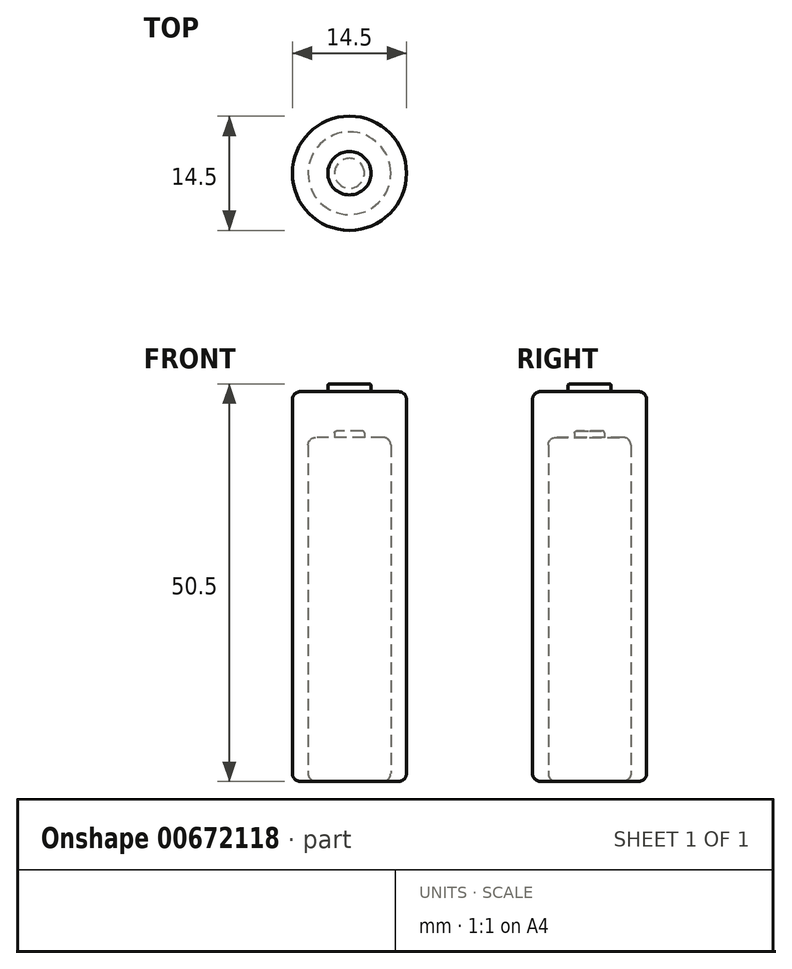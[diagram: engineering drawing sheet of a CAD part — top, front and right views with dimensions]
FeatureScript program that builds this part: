
annotation { "Feature Type Name" : "Feature", "Feature Type Description" : "" }
export const myFeature = defineFeature(function(context is Context, id is Id, definition is map)
    precondition{}
    {
        {
            var Q0;
            Q0=qCreatedBy(makeId("Top.planeOp"),FACE);
            var sketch = newSketch(context, id + "F0", { "sketchPlane" : qUnion([Q0])});
            skCircle(sketch, "E0", {"center": v(0, 0) * mm, "radius": 5.25 * mm});
            skSolve(sketch);
        }
        {
            var Q0;
            Q0=makeQuery(id+"F0.imprint","IMPRINT",FACE,{"disambiguationData":[TD([[makeQuery(id+"F0.imprint","IMPRINT",EDGE,{"derivedFrom":sQuery(id+"F0.wireOp",EDGE,"E0")}),1.0]])]});
            extrude(context, id + "F1", {"entities" : qUnion([Q0]), "depth" : (44.5 - .8) * mm, "offsetDistance" : 25 * mm});
        }
        {
            var Q0;
            Q0=makeQuery(id+"F1.opExtrude","CAP_FACE",FACE,{"disambiguationData":[OSD([sQuery(id+"F0.wireOp",EDGE,"E0")])],"isStart":false});
            var sketch = newSketch(context, id + "F2", { "sketchPlane" : qUnion([Q0])});
            skCircle(sketch, "E1", {"center": v(0, 0) * mm, "radius": 1.9 * mm});
            skSolve(sketch);
        }
        {
            var Q0;
            Q0=makeQuery(id+"F2.imprint","IMPRINT",FACE,{"disambiguationData":[TD([[makeQuery(id+"F2.imprint","IMPRINT",EDGE,{"derivedFrom":sQuery(id+"F2.wireOp",EDGE,"E1")}),1.0]])]});
            extrude(context, id + "F3", {"entities" : qUnion([Q0]), "operationType" : NewBodyOperationType.ADD, "depth" : .8 * mm, "offsetDistance" : 25 * mm});
        }
        {
            var Q0;
            Q0=makeQuery(id+"F3.opExtrude","CAP_EDGE",EDGE,{"disambiguationData":[OSD([sQuery(id+"F2.wireOp",EDGE,"E1")])],"isStart":true});
            var Q1;
            Q1=makeQuery(id+"F3.opExtrude","CAP_EDGE",EDGE,{"disambiguationData":[OSD([sQuery(id+"F2.wireOp",EDGE,"E1")])],"isStart":false});
            fillet(context, id + "F4", {"entities" : qUnion([Q0, Q1]), "radius" : .25 * mm, "tangentPropagation" : true, "allowEdgeOverflow" : false});
        }
        {
            var Q0;
            Q0=makeQuery(id+"F1.opExtrude","CAP_EDGE",EDGE,{"disambiguationData":[OSD([sQuery(id+"F0.wireOp",EDGE,"E0")])],"isStart":false});
            var Q1;
            Q1=makeQuery(id+"F1.opExtrude","CAP_EDGE",EDGE,{"disambiguationData":[OSD([sQuery(id+"F0.wireOp",EDGE,"E0")])],"isStart":true});
            fillet(context, id + "F5", {"entities" : qUnion([Q0, Q1]), "radius" : 1 * mm, "tangentPropagation" : true, "allowEdgeOverflow" : false});
        }
        {
            var Q0;
            Q0=qCreatedBy(makeId("Top.planeOp"),FACE);
            var sketch = newSketch(context, id + "F6", { "sketchPlane" : qUnion([Q0])});
            skCircle(sketch, "E2", {"center": v(0, 0) * mm, "radius": 7.25 * mm});
            skSolve(sketch);
        }
        {
            var Q0;
            Q0=makeQuery(id+"F6.imprint","IMPRINT",FACE,{"disambiguationData":[TD([[makeQuery(id+"F6.imprint","IMPRINT",EDGE,{"derivedFrom":sQuery(id+"F6.wireOp",EDGE,"E2")}),1.0]])]});
            extrude(context, id + "F7", {"entities" : qUnion([Q0]), "depth" : 49.5 * mm, "offsetDistance" : 25 * mm});
        }
        {
            var Q0;
            Q0=makeQuery(id+"F7.opExtrude","CAP_FACE",FACE,{"disambiguationData":[OSD([sQuery(id+"F6.wireOp",EDGE,"E2")])],"isStart":false});
            var sketch = newSketch(context, id + "F8", { "sketchPlane" : qUnion([Q0])});
            skCircle(sketch, "E3", {"center": v(0, 0) * mm, "radius": 2.75 * mm});
            skSolve(sketch);
        }
        {
            var Q0;
            Q0=makeQuery(id+"F8.imprint","IMPRINT",FACE,{"disambiguationData":[TD([[makeQuery(id+"F8.imprint","IMPRINT",EDGE,{"derivedFrom":sQuery(id+"F8.wireOp",EDGE,"E3")}),1.0]])]});
            extrude(context, id + "F9", {"entities" : qUnion([Q0]), "operationType" : NewBodyOperationType.ADD, "depth" : 1 * mm, "offsetDistance" : 25 * mm});
        }
        {
            var Q0;
            Q0=makeQuery(id+"F9.opExtrude","CAP_EDGE",EDGE,{"disambiguationData":[OSD([sQuery(id+"F8.wireOp",EDGE,"E3")])],"isStart":false});
            var Q1;
            Q1=makeQuery(id+"F9.opExtrude","CAP_EDGE",EDGE,{"disambiguationData":[OSD([sQuery(id+"F8.wireOp",EDGE,"E3")])],"isStart":true});
            fillet(context, id + "F10", {"entities" : qUnion([Q0, Q1]), "radius" : .25 * mm, "tangentPropagation" : true, "allowEdgeOverflow" : false});
        }
        {
            var Q0;
            Q0=makeQuery(id+"F7.opExtrude","CAP_EDGE",EDGE,{"disambiguationData":[OSD([sQuery(id+"F6.wireOp",EDGE,"E2")])],"isStart":false});
            var Q1;
            Q1=makeQuery(id+"F7.opExtrude","CAP_EDGE",EDGE,{"disambiguationData":[OSD([sQuery(id+"F6.wireOp",EDGE,"E2")])],"isStart":true});
            fillet(context, id + "F11", {"entities" : qUnion([Q0, Q1]), "radius" : 1 * mm, "tangentPropagation" : true, "allowEdgeOverflow" : false});
        }
    });
